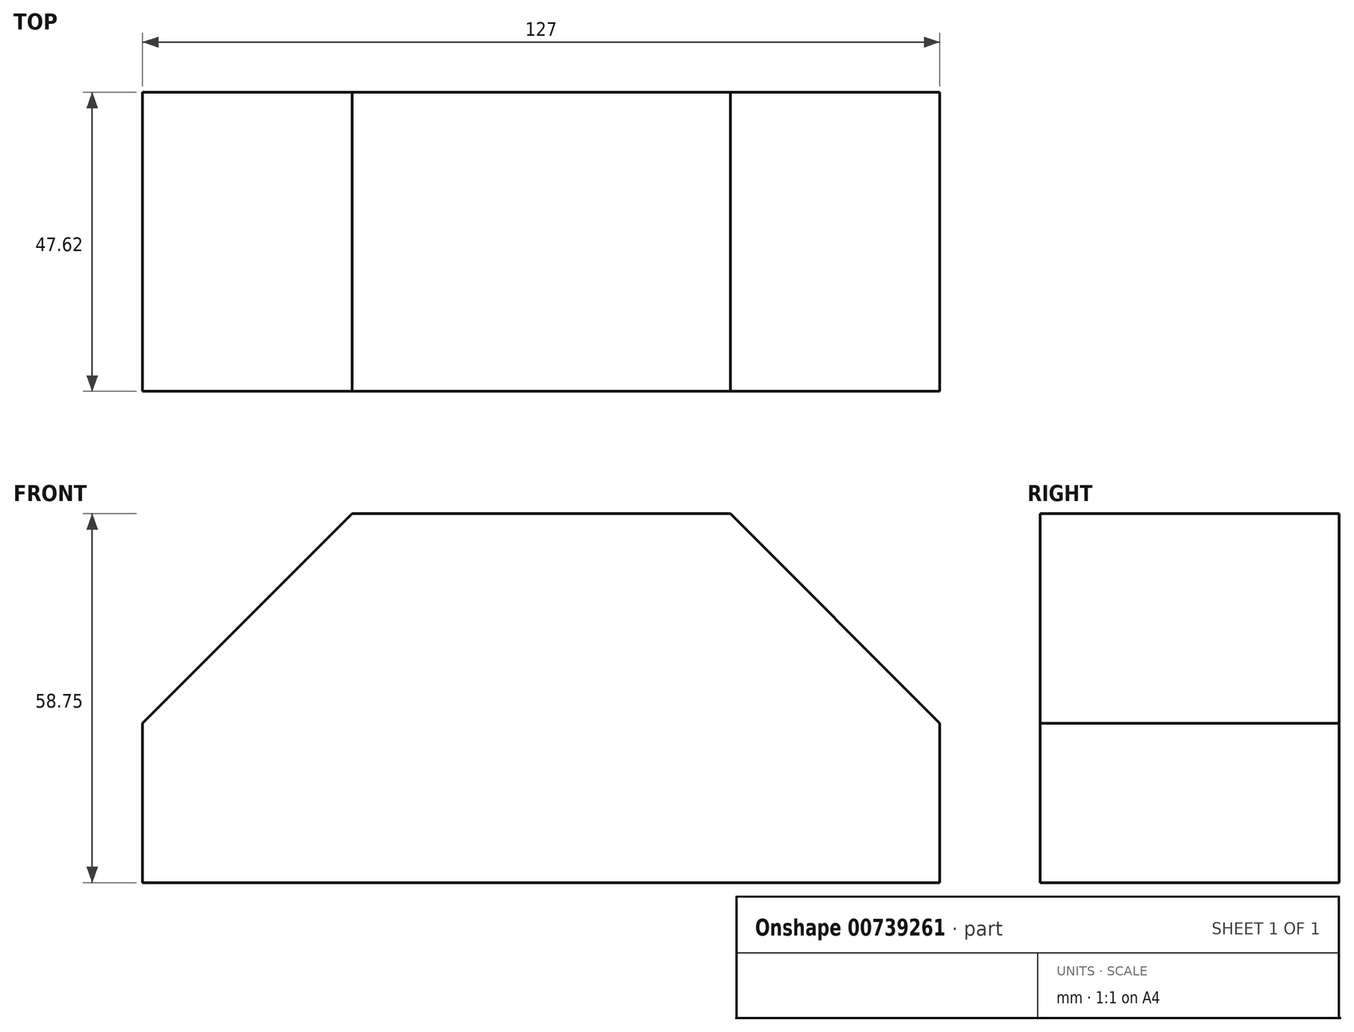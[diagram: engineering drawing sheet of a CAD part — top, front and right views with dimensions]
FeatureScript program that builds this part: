
annotation { "Feature Type Name" : "Feature", "Feature Type Description" : "" }
export const myFeature = defineFeature(function(context is Context, id is Id, definition is map)
    precondition{}
    {
        {
            var Q0;
            Q0=qCreatedBy(makeId("Front.planeOp"),FACE);
            var sketch = newSketch(context, id + "F0", { "sketchPlane" : qUnion([Q0])});
            skLineSegment(sketch, "E0", {"start": v(0, 0) * mm, "end": v(-127, 0) * mm});
            skLineSegment(sketch, "E1", {"start": v(-127, 0) * mm, "end": v(-127, 25.4) * mm});
            skLineSegment(sketch, "E2", {"start": v(-127, 25.4) * mm, "end": v(-93.65, 58.75) * mm});
            skLineSegment(sketch, "E3", {"start": v(-93.65, 58.75) * mm, "end": v(-33.35, 58.75) * mm});
            skLineSegment(sketch, "E4", {"start": v(-33.35, 58.75) * mm, "end": v(0, 25.4) * mm});
            skLineSegment(sketch, "E5", {"start": v(0, 25.4) * mm, "end": v(0, 0) * mm});
            skSolve(sketch);
        }
        {
            var Q0;
            Q0 = qSketchRegion(id + "F0", true);
            extrude(context, id + "F1", {"entities" : qUnion([Q0]), "depth" : 47.62 * mm, "offsetDistance" : 25.4 * mm});
        }
    });
